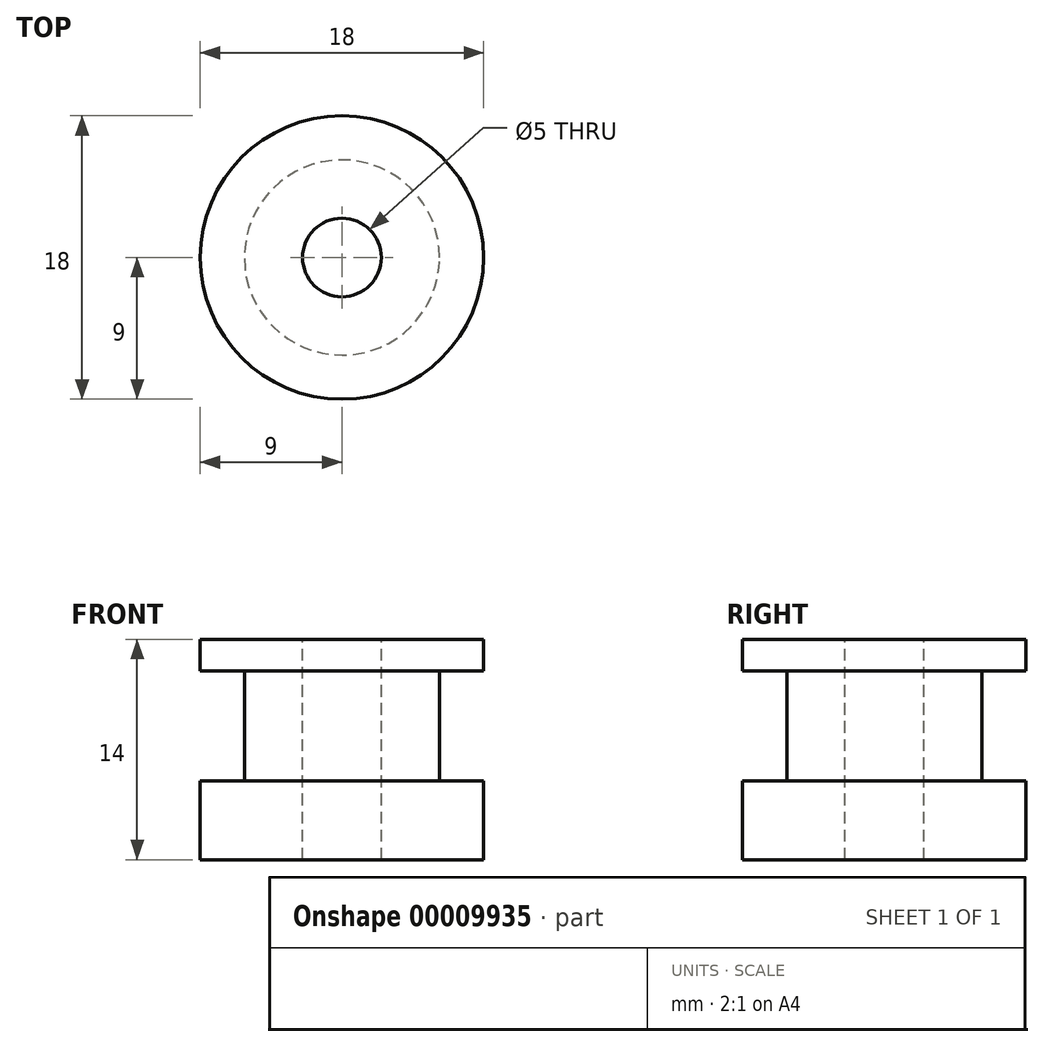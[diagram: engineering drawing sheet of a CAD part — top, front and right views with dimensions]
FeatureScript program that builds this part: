
annotation { "Feature Type Name" : "Feature", "Feature Type Description" : "" }
export const myFeature = defineFeature(function(context is Context, id is Id, definition is map)
    precondition{}
    {
        {
            var Q0;
            Q0=qCreatedBy(makeId("Top.planeOp"),FACE);
            var sketch = newSketch(context, id + "F0", { "sketchPlane" : qUnion([Q0])});
            skCircle(sketch, "E0", {"center": v(0, 0) * mm, "radius": 9 * mm});
            skSolve(sketch);
        }
        {
            var Q0;
            Q0=qSketchRegion(id+"F0",true);
            extrude(context, id + "F1", {"entities" : qUnion([Q0]), "depth" : 5 * mm});
        }
        {
            var Q0;
            Q0=makeQuery(id+"F1.opExtrude","CAP_FACE",FACE,{"disambiguationData":[OSD([sQuery(id+"F0.wireOp",EDGE,"E0")])],"isStart":false});
            var sketch = newSketch(context, id + "F2", { "sketchPlane" : qUnion([Q0])});
            skCircle(sketch, "E1", {"center": v(0, 0) * mm, "radius": 6.2 * mm});
            skSolve(sketch);
        }
        {
            var Q0;
            Q0=qSketchRegion(id+"F2",true);
            extrude(context, id + "F3", {"entities" : qUnion([Q0]), "operationType" : NewBodyOperationType.ADD, "depth" : 7 * mm});
        }
        {
            var Q0;
            Q0=makeQuery(id+"F3.opExtrude","CAP_FACE",FACE,{"disambiguationData":[OSD([sQuery(id+"F2.wireOp",EDGE,"E1")])],"isStart":false});
            var sketch = newSketch(context, id + "F4", { "sketchPlane" : qUnion([Q0])});
            skCircle(sketch, "E2", {"center": v(0, 0) * mm, "radius": 9 * mm});
            skSolve(sketch);
        }
        {
            var Q0;
            Q0=qSketchRegion(id+"F4",true);
            extrude(context, id + "F5", {"entities" : qUnion([Q0]), "operationType" : NewBodyOperationType.ADD, "depth" : 2 * mm});
        }
        {
            var Q0;
            Q0=makeQuery(id+"F5.opExtrude","CAP_FACE",FACE,{"disambiguationData":[OSD([sQuery(id+"F4.wireOp",EDGE,"E2")])],"isStart":false});
            var sketch = newSketch(context, id + "F6", { "sketchPlane" : qUnion([Q0])});
            skCircle(sketch, "E3", {"center": v(0, 0) * mm, "radius": 2.5 * mm});
            skSolve(sketch);
        }
        {
            var Q0;
            Q0=qSketchRegion(id+"F6",true);
            extrude(context, id + "F7", {"entities" : qUnion([Q0]), "operationType" : NewBodyOperationType.REMOVE, "oppositeDirection" : true, "depth" : 25 * mm});
        }
    });
